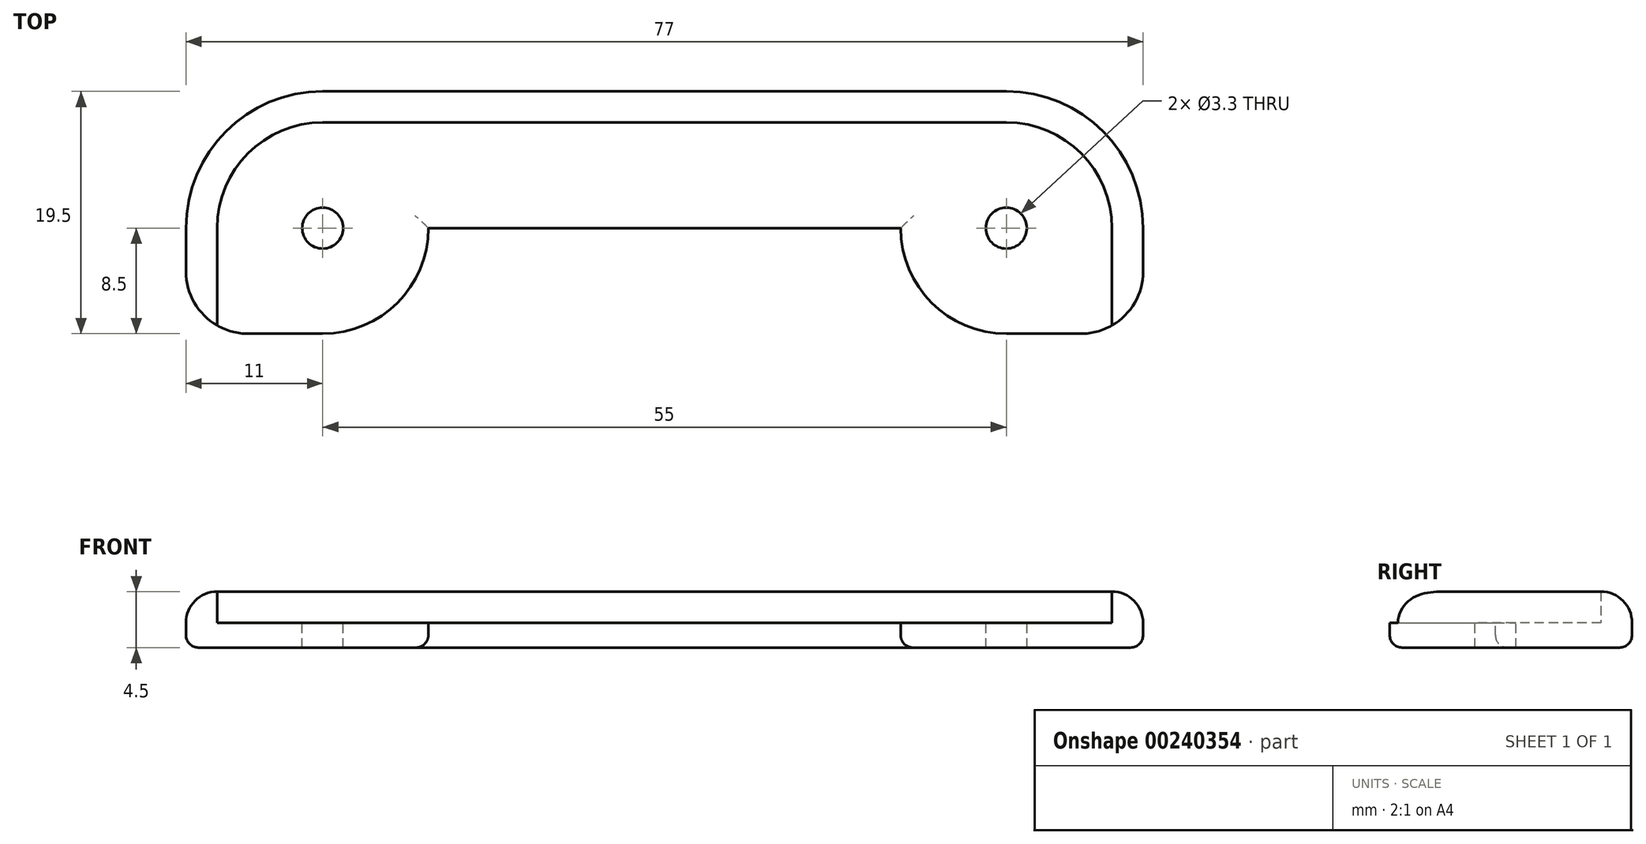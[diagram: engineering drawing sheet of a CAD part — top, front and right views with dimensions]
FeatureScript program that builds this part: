
annotation { "Feature Type Name" : "Feature", "Feature Type Description" : "" }
export const myFeature = defineFeature(function(context is Context, id is Id, definition is map)
    precondition{}
    {
        {
            var Q0;
            Q0=qCreatedBy(makeId("Top.planeOp"),FACE);
            var sketch = newSketch(context, id + "F0", { "sketchPlane" : qUnion([Q0])});
            skArc(sketch, "E0", {"start": v(-27.5, 8.5) * mm, "mid": v(-33.51, 6.01) * mm, "end": v(-36, 0) * mm});
            skArc(sketch, "E1.MirrorC", {"start": v(27.5, 8.5) * mm, "mid": v(33.51, 6.01) * mm, "end": v(36, 0) * mm});
            skLineSegment(sketch, "E2.bottom", {"start": v(19, 0) * mm, "end": v(-19, 0) * mm});
            skLineSegment(sketch, "E2.top", {"start": v(27.5, 8.5) * mm, "end": v(-27.5, 8.5) * mm});
            skPoint(sketch, "E3", {"position": v(-36, 0) * mm});
            skPoint(sketch, "E4", {"position": v(36, 0) * mm});
            skLineSegment(sketch, "E5.top", {"start": v(36, -8.5) * mm, "end": v(27.5, -8.5) * mm});
            skLineSegment(sketch, "E5.left", {"start": v(36, 0) * mm, "end": v(36, -8.5) * mm});
            skLineSegment(sketch, "E6.bottom", {"start": v(-27.5, -8.5) * mm, "end": v(-36, -8.5) * mm});
            skLineSegment(sketch, "E6.right", {"start": v(-36, -8.5) * mm, "end": v(-36, 0) * mm});
            skArc(sketch, "E7.trimOffspring", {"start": v(-27.5, -8.5) * mm, "mid": v(-21.49, -6.01) * mm, "end": v(-19, 0) * mm});
            skArc(sketch, "E8.trimOffspring", {"start": v(27.5, -8.5) * mm, "mid": v(21.49, -6.01) * mm, "end": v(19, 0) * mm});
            skLineSegment(sketch, "E9.0", {"start": v(-38.5, -8.5) * mm, "end": v(-38.5, 0) * mm});
            skLineSegment(sketch, "E9.1", {"start": v(38.5, 0) * mm, "end": v(38.5, -8.5) * mm});
            skArc(sketch, "E9.2", {"start": v(27.5, 11) * mm, "mid": v(35.28, 7.78) * mm, "end": v(38.5, 0) * mm});
            skLineSegment(sketch, "E9.3", {"start": v(27.5, 11) * mm, "end": v(-27.5, 11) * mm});
            skArc(sketch, "E9.4", {"start": v(-27.5, 11) * mm, "mid": v(-35.28, 7.78) * mm, "end": v(-38.5, 0) * mm});
            skLineSegment(sketch, "E10", {"start": v(-38.5, -8.5) * mm, "end": v(-36, -8.5) * mm});
            skLineSegment(sketch, "E11", {"start": v(36, -8.5) * mm, "end": v(38.5, -8.5) * mm});
            skSolve(sketch);
        }
        {
            var Q0;
            Q0=makeQuery(id+"F0.imprint","IMPRINT",FACE,{"disambiguationData":[TD([[makeQuery(id+"F0.imprint","IMPRINT",EDGE,{"derivedFrom":sQuery(id+"F0.wireOp",EDGE,"E0")}),-1.0]])]});
            extrude(context, id + "F1", {"entities" : qUnion([Q0]), "depth" : 2.5 * mm});
        }
        {
            var Q0;
            Q0=makeQuery(id+"F0.imprint","IMPRINT",FACE,{"disambiguationData":[TD([[makeQuery(id+"F0.imprint","IMPRINT",EDGE,{"derivedFrom":sQuery(id+"F0.wireOp",EDGE,"E0")}),-1.0]])]});
            var Q1;
            Q1=makeQuery(id+"F0.imprint","IMPRINT",FACE,{"disambiguationData":[TD([[makeQuery(id+"F0.imprint","IMPRINT",EDGE,{"derivedFrom":sQuery(id+"F0.wireOp",EDGE,"E0")}),1.0]])]});
            extrude(context, id + "F2", {"entities" : qUnion([Q0, Q1]), "operationType" : NewBodyOperationType.ADD, "oppositeDirection" : true, "depth" : 2 * mm});
        }
        {
            var Q0;
            Q0=sQuery(id+"F0.wireOp",VERTEX,"E1.MirrorC.center");
            var Q1;
            Q1=sQuery(id+"F0.wireOp",VERTEX,"E0.center");
            var Q2;
            Q2=makeQuery(id+"F1.opExtrude","SWEPT_BODY",BODY,{"disambiguationData":[OSD([sQuery(id+"F0.wireOp",EDGE,"E0"),sQuery(id+"F0.wireOp",EDGE,"E1.MirrorC"),sQuery(id+"F0.wireOp",EDGE,"E2.top"),sQuery(id+"F0.wireOp",EDGE,"E5.left"),sQuery(id+"F0.wireOp",EDGE,"E6.right"),sQuery(id+"F0.wireOp",EDGE,"E9.0"),sQuery(id+"F0.wireOp",EDGE,"E9.1"),sQuery(id+"F0.wireOp",EDGE,"E9.2"),sQuery(id+"F0.wireOp",EDGE,"E9.3"),sQuery(id+"F0.wireOp",EDGE,"E9.4"),sQuery(id+"F0.wireOp",EDGE,"E10"),sQuery(id+"F0.wireOp",EDGE,"E11")])]});
            hole(context, id + "F3", {"style" : HoleStyle.SIMPLE, "endStyle" : HoleEndStyle.THROUGH, "standardTappedOrClearance" : lookupTablePath({ "standard" : "ISO", "fit" : "Normal", "size" : "M3", "type" : "Clearance" }), "standardBlindInLast" : lookupTablePath({ "fit" : "Standard", "standard" : "ISO", "size" : "M3", "type" : "Clearance" }), "holeDiameter" : 3.3 * mm, "tappedDepth" : 13.9 * mm, "tapClearance" : 3, "startFromSketch" : true, "locations" : qUnion([Q0, Q1]), "scope" : qUnion([Q2])});
        }
        {
            var Q0;
            {var subQ0=sQuery(id+"F0.wireOp",EDGE,"E10");var subQ1=sQuery(id+"F0.wireOp",EDGE,"E9.0");Q0=makeQuery(id+"F2.boolean.opBoolean","MERGE",EDGE,{"derivedFrom":[makeQuery(id+"F1.opExtrude","SWEPT_EDGE",EDGE,{"disambiguationData":[OSD([subQ1,subQ0])]}),makeQuery(id+"F2.opExtrude","SWEPT_EDGE",EDGE,{"disambiguationData":[OSD([subQ1,subQ0])]})]});}
            var Q1;
            {var subQ0=sQuery(id+"F0.wireOp",EDGE,"E11");var subQ1=sQuery(id+"F0.wireOp",EDGE,"E9.1");Q1=makeQuery(id+"F2.boolean.opBoolean","MERGE",EDGE,{"derivedFrom":[makeQuery(id+"F1.opExtrude","SWEPT_EDGE",EDGE,{"disambiguationData":[OSD([subQ1,subQ0])]}),makeQuery(id+"F2.opExtrude","SWEPT_EDGE",EDGE,{"disambiguationData":[OSD([subQ1,subQ0])]})]});}
            fillet(context, id + "F4", {"entities" : qUnion([Q0, Q1]), "radius" : 5 * mm, "tangentPropagation" : true, "allowEdgeOverflow" : false});
        }
        {
            var Q0;
            Q0=makeQuery(id+"F1.opExtrude","CAP_EDGE",EDGE,{"disambiguationData":[OSD([sQuery(id+"F0.wireOp",EDGE,"E9.3")])],"isStart":false});
            fillet(context, id + "F5", {"entities" : qUnion([Q0]), "radius" : 2.5 * mm, "tangentPropagation" : true, "allowEdgeOverflow" : false});
        }
        {
            var Q0;
            Q0=makeQuery(id+"F2.opExtrude","CAP_EDGE",EDGE,{"disambiguationData":[OSD([sQuery(id+"F0.wireOp",EDGE,"E9.3")])],"isStart":false});
            var Q1;
            Q1=makeQuery(id+"F2.opExtrude","CAP_EDGE",EDGE,{"disambiguationData":[OSD([sQuery(id+"F0.wireOp",EDGE,"E2.bottom")])],"isStart":false});
            fillet(context, id + "F6", {"entities" : qUnion([Q0, Q1]), "radius" : 1 * mm, "tangentPropagation" : true, "allowEdgeOverflow" : false});
        }
    });
